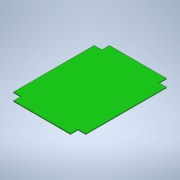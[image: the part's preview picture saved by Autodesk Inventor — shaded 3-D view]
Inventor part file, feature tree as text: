
AUTODESK INVENTOR PART (.ipt)
format: ipt  version: 2022 (Build 260153000, 153)  size: 129,536 bytes
history: native  units: in
note: dims shown in document units (in); Inventor stores cm internally (conversion verified against a paired STEP export)
features: extrude x2, sketch x2
ambient origin geometry x8: Origin, YZ Plane, XZ Plane, XY Plane, X Axis, Y Axis, Z Axis, Center Point
bodies: Solid1 (feature_tree)
feature tree (4):
  extrude  "Extrusion1"  Depth=2.2244in
  extrude  "Extrusion2"  Depth=0.1772in
  sketch  "Sketch1"  dims[d0=1.6772in d1=2.2244in]
  sketch  "Sketch5"  dims[d2=0.0197in d3=0.0in d23=0.1772in d24=0.1752in d25=0.1752in d26=0.1752in d27=0.1752in d28=0.1772in d29=0.1772in d30=0.1772in d31=0.0in d32=0.0in]
